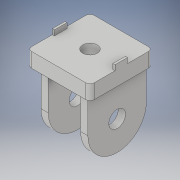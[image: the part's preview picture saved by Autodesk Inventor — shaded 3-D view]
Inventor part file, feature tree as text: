
AUTODESK INVENTOR PART (.ipt)
format: ipt  version: 2018 (Build 220112000, 112)  size: 190,464 bytes
history: native  units: mm
features: extrude x5, sketch x5, projected_geometry x2, hole x1
ambient origin geometry x8: Origin, YZ Plane, XZ Plane, XY Plane, X Axis, Y Axis, Z Axis, Center Point
bodies: Volumenkörper1 (feature_tree)
feature tree (13):
  extrude  "Extrusion1"  Depth=3.0mm
  extrude  "Extrusion2"  Depth=0.7mm
  extrude  "Extrusion3"  Depth=0.6mm
  extrude  "Extrusion4"  Depth=0.6mm
  extrude  "Extrusion5"  Depth=0.6mm
  hole  "Bohrung1"  [1 undecoded]
  sketch  "Skizze1"  dims[d0=3.0mm d1=3.0mm]
  projected_geometry  "Projizierte Kontur1"
  sketch  "Skizze3"  dims[d2=0.2mm d3=0.7mm]
  projected_geometry  "Projizierte Kontur2"
  sketch  "Skizze4"  dims[d4=0.7mm d5=0.0mm d6=0.6mm]
  sketch  "Skizze5"  dims[d7=0.1mm d8=0.6mm]
  sketch  "Skizze6"  dims[d9=0.6mm d10=0.6mm d11=0.1mm d12=0.1mm d13=0.1mm d14=0.25mm d15=0.0mm d16=0.35mm d17=0.35mm d18=2.8mm d19=0.2mm d20=0.55mm d21=1.55mm d22=0.0mm d23=0.35mm d24=0.0mm d25=0.35mm d26=0.0mm d27=0.8mm d28=6.0mm d29=4.0mm d30=2.0mm d31=90.0deg d32=8.0mm d33=20.594885mm]
note: 1 required parameter value undecoded (feature->parameter linkage not recoverable at this tier; creation-order binding heuristic only, values carry confidence <= 0.55)
